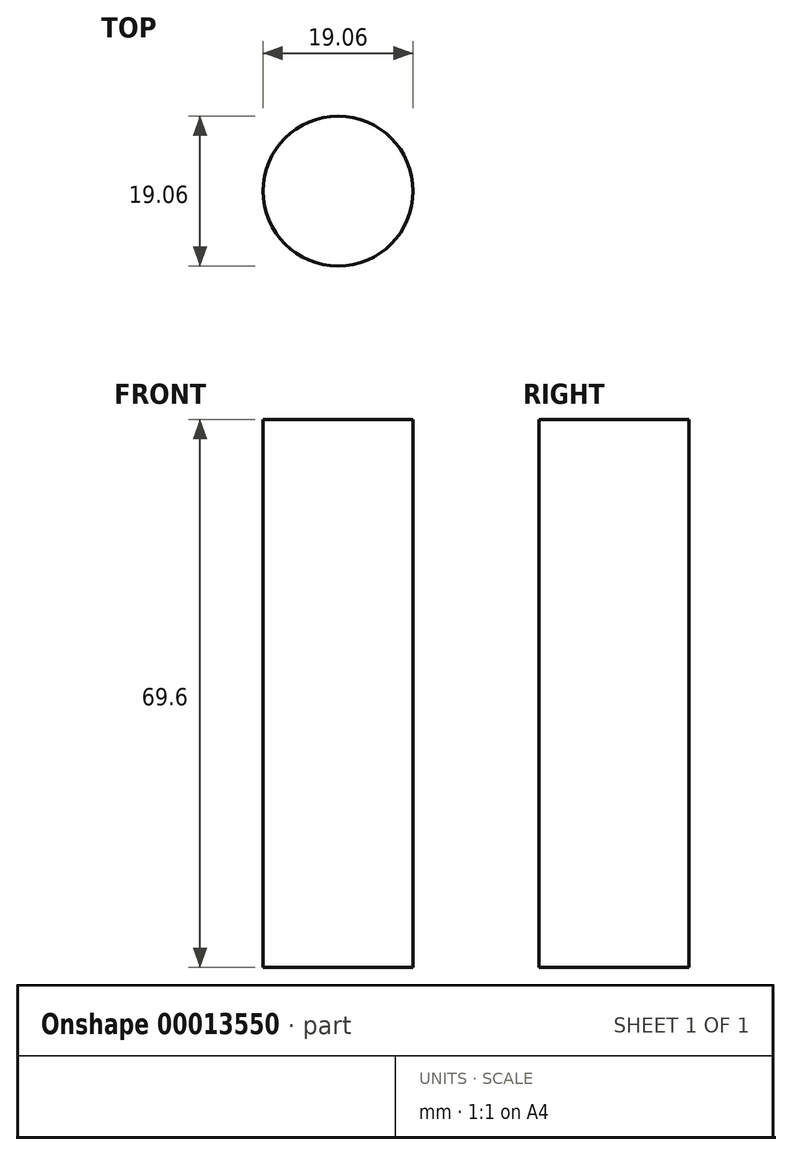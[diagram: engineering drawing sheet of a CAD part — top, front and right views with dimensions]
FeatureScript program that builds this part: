
annotation { "Feature Type Name" : "Feature", "Feature Type Description" : "" }
export const myFeature = defineFeature(function(context is Context, id is Id, definition is map)
    precondition{}
    {
        {
            var Q0;
            Q0=qCreatedBy(makeId("Top.planeOp"),FACE);
            var sketch = newSketch(context, id + "F0", { "sketchPlane" : qUnion([Q0])});
            skCircle(sketch, "E0", {"center": v(0, 0) * mm, "radius": 9.53 * mm});
            skSolve(sketch);
        }
        {
            var Q0;
            Q0 = qSketchRegion(id + "F0", true);
            extrude(context, id + "F1", {"entities" : qUnion([Q0]), "depth" : 69.6 * mm});
        }
    });
